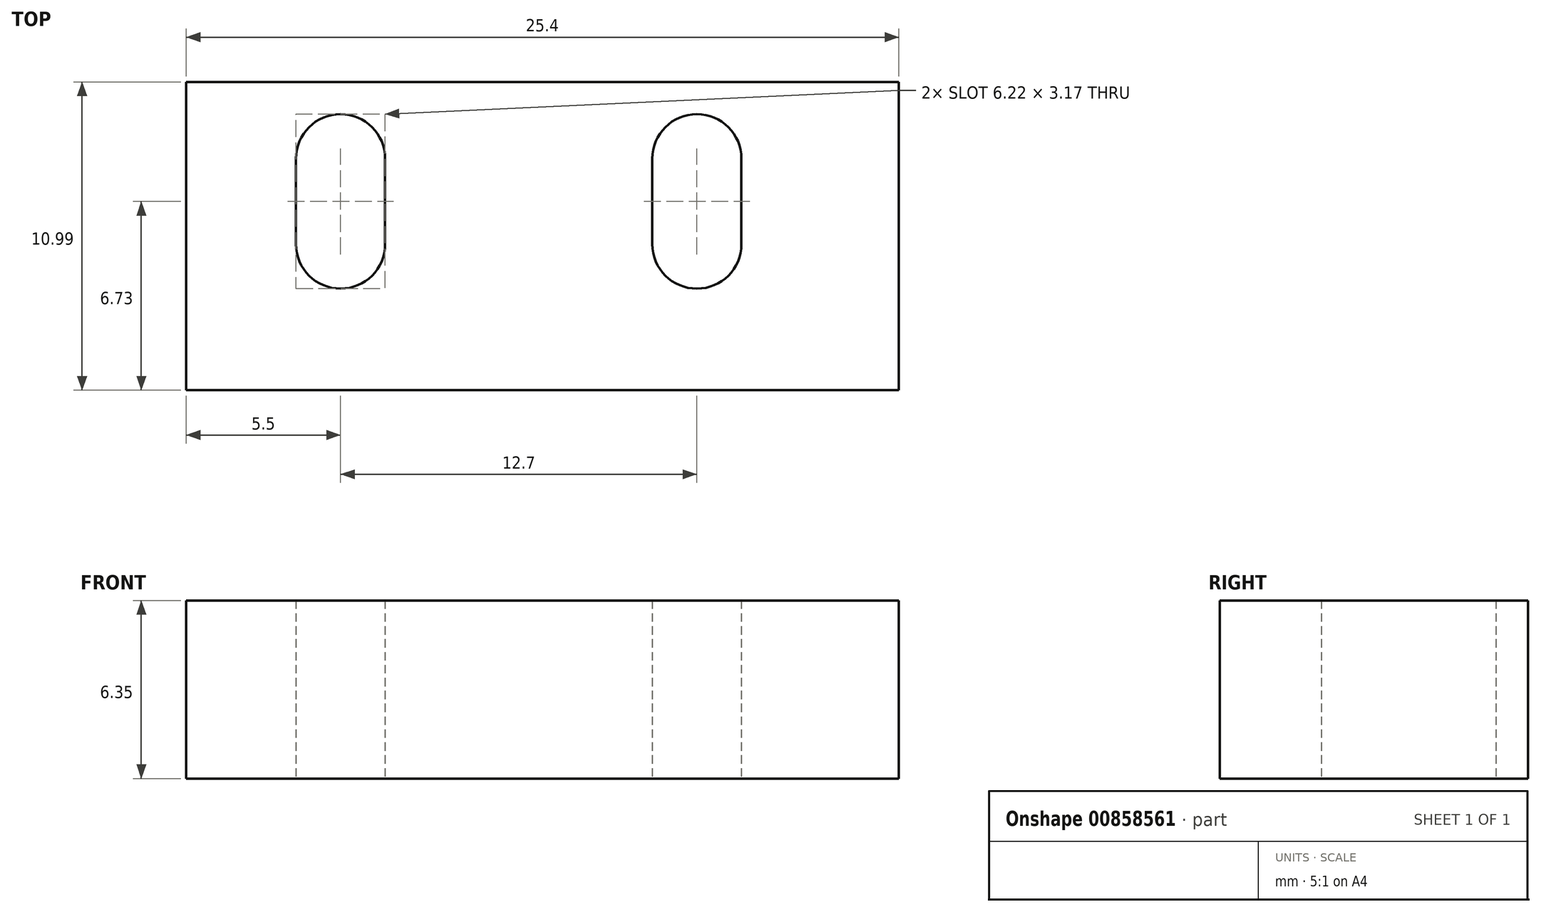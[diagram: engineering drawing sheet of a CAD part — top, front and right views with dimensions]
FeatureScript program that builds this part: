
annotation { "Feature Type Name" : "Feature", "Feature Type Description" : "" }
export const myFeature = defineFeature(function(context is Context, id is Id, definition is map)
    precondition{}
    {
        {
            var Q0;
            Q0=qCreatedBy(makeId("Top.planeOp"),FACE);
            var sketch = newSketch(context, id + "F0", { "sketchPlane" : qUnion([Q0])});
            skLineSegment(sketch, "E0.bottom", {"start": v(-11.85, 4.26) * mm, "end": v(13.55, 4.26) * mm});
            skLineSegment(sketch, "E0.top", {"start": v(-11.85, -6.73) * mm, "end": v(13.55, -6.73) * mm});
            skLineSegment(sketch, "E0.left", {"start": v(-11.85, 4.26) * mm, "end": v(-11.85, -6.73) * mm});
            skLineSegment(sketch, "E0.right", {"start": v(13.55, 4.26) * mm, "end": v(13.55, -6.73) * mm});
            skCircle(sketch, "E1", {"center": v(-6.35, 0) * mm, "radius": 1.59 * mm});
            skCircle(sketch, "E2.MirrorC", {"center": v(6.35, 0) * mm, "radius": 1.59 * mm});
            skLineSegment(sketch, "E3.bottom", {"start": v(-53.3, 42.77) * mm, "end": v(-31.81, 42.77) * mm});
            skLineSegment(sketch, "E3.top", {"start": v(-53.3, 35.1) * mm, "end": v(-31.81, 35.1) * mm});
            skLineSegment(sketch, "E3.left", {"start": v(-53.3, 42.77) * mm, "end": v(-53.3, 35.1) * mm});
            skLineSegment(sketch, "E3.right", {"start": v(-31.81, 42.77) * mm, "end": v(-31.81, 35.1) * mm});
            skLineSegment(sketch, "E4", {"start": v(-6.35, 0) * mm, "end": v(-6.35, 1.52) * mm});
            skLineSegment(sketch, "E5.MirrorCS", {"start": v(-6.35, 0) * mm, "end": v(-6.35, -1.52) * mm});
            skLineSegment(sketch, "E6.MirrorCS", {"start": v(6.35, 0) * mm, "end": v(6.35, 1.52) * mm});
            skLineSegment(sketch, "E7.MirrorCS", {"start": v(6.35, 0) * mm, "end": v(6.35, -1.52) * mm});
            skArc(sketch, "E8.0.startCap", {"start": v(-4.76, 0) * mm, "mid": v(-6.35, -1.59) * mm, "end": v(-7.94, 0) * mm});
            skArc(sketch, "E8.0.endCap", {"start": v(-7.94, 1.52) * mm, "mid": v(-6.35, 3.11) * mm, "end": v(-4.76, 1.52) * mm});
            skLineSegment(sketch, "E8.0.left", {"start": v(-7.94, 0) * mm, "end": v(-7.94, 1.52) * mm});
            skLineSegment(sketch, "E8.0.right", {"start": v(-4.76, 0) * mm, "end": v(-4.76, 1.52) * mm});
            skArc(sketch, "E8.1.startCap", {"start": v(-7.94, 0) * mm, "mid": v(-6.35, 1.59) * mm, "end": v(-4.76, 0) * mm});
            skArc(sketch, "E8.1.endCap", {"start": v(-4.76, -1.52) * mm, "mid": v(-6.35, -3.11) * mm, "end": v(-7.94, -1.52) * mm});
            skLineSegment(sketch, "E8.1.left", {"start": v(-4.76, 0) * mm, "end": v(-4.76, -1.52) * mm});
            skLineSegment(sketch, "E8.1.right", {"start": v(-7.94, 0) * mm, "end": v(-7.94, -1.52) * mm});
            skArc(sketch, "E9.MirrorCS", {"start": v(4.76, 0) * mm, "mid": v(6.35, -1.59) * mm, "end": v(7.94, 0) * mm});
            skLineSegment(sketch, "E10.MirrorCS", {"start": v(7.94, 0) * mm, "end": v(7.94, 1.52) * mm});
            skArc(sketch, "E11.MirrorCS", {"start": v(7.94, 0) * mm, "mid": v(6.35, 1.59) * mm, "end": v(4.76, 0) * mm});
            skArc(sketch, "E12.MirrorCS", {"start": v(4.76, -1.52) * mm, "mid": v(6.35, -3.11) * mm, "end": v(7.94, -1.52) * mm});
            skArc(sketch, "E13.MirrorCS", {"start": v(7.94, 1.52) * mm, "mid": v(6.35, 3.11) * mm, "end": v(4.76, 1.52) * mm});
            skLineSegment(sketch, "E14.MirrorCS", {"start": v(4.76, 0) * mm, "end": v(4.76, 1.52) * mm});
            skLineSegment(sketch, "E15.MirrorCS", {"start": v(7.94, 0) * mm, "end": v(7.94, -1.52) * mm});
            skLineSegment(sketch, "E16.MirrorCS", {"start": v(4.76, 0) * mm, "end": v(4.76, -1.52) * mm});
            skSolve(sketch);
        }
        {
            var Q0;
            Q0=makeQuery(id+"F0.imprint","IMPRINT",FACE,{"disambiguationData":[TD([[makeQuery(id+"F0.imprint","IMPRINT",EDGE,{"derivedFrom":sQuery(id+"F0.wireOp",EDGE,"E0.bottom")}),-1.0]])]});
            extrude(context, id + "F1", {"entities" : qUnion([Q0]), "depth" : 6.35 * mm, "offsetDistance" : 25.4 * mm});
        }
    });
